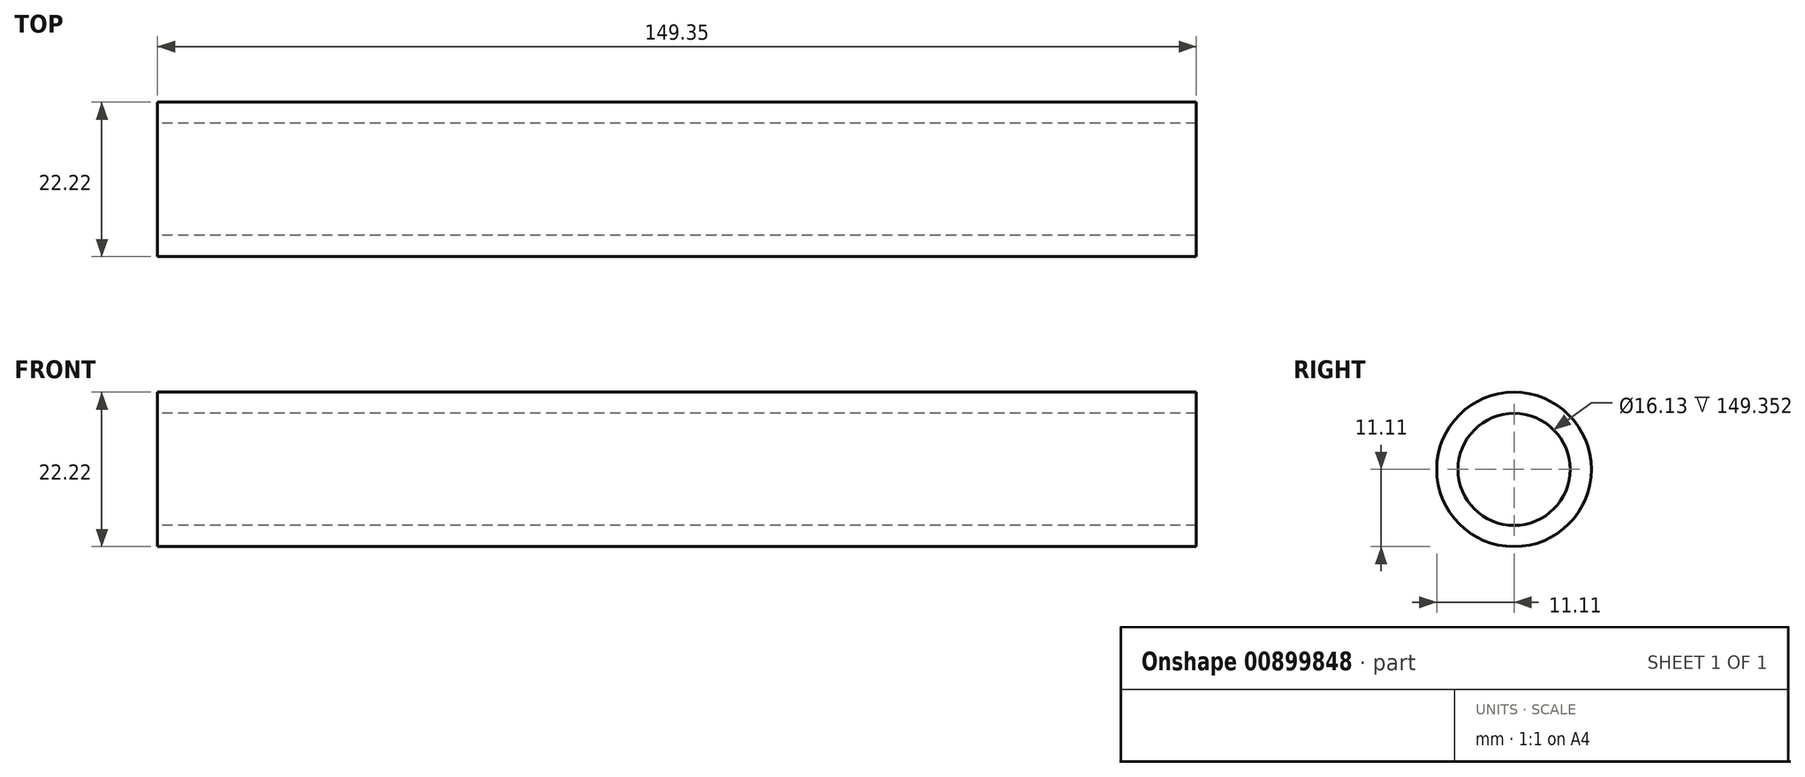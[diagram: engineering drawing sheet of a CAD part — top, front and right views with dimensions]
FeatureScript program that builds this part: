
annotation { "Feature Type Name" : "Feature", "Feature Type Description" : "" }
export const myFeature = defineFeature(function(context is Context, id is Id, definition is map)
    precondition{}
    {
        {
            var Q0;
            Q0=qCreatedBy(makeId("Right.planeOp"),FACE);
            var sketch = newSketch(context, id + "F0", { "sketchPlane" : qUnion([Q0])});
            skCircle(sketch, "E0", {"center": v(0, 0) * mm, "radius": 11.11 * mm});
            skSolve(sketch);
        }
        {
            var Q0;
            Q0 = qSketchRegion(id + "F0", true);
            extrude(context, id + "F1", {"entities" : qUnion([Q0]), "depth" : 149.35 * mm, "offsetDistance" : 25.4 * mm});
        }
        {
            var Q0;
            Q0=makeQuery(id+"F1.opExtrude","CAP_FACE",FACE,{"disambiguationData":[OSD([sQuery(id+"F0.wireOp",EDGE,"E0")])],"isStart":false});
            var Q1;
            Q1=makeQuery(id+"F1.opExtrude","CAP_FACE",FACE,{"disambiguationData":[OSD([sQuery(id+"F0.wireOp",EDGE,"E0")])],"isStart":true});
            shell(context, id + "F2", {"entities" : qUnion([Q0, Q1]), "thickness" : 3.05 * mm});
        }
    });
